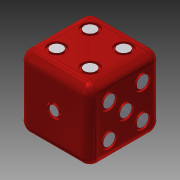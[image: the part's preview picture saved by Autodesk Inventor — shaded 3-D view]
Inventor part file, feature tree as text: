
AUTODESK INVENTOR PART (.ipt)
format: ipt  version: 2013 (Build 170138000, 138)  size: 348,160 bytes
history: native  units: mm
features: extrude x14, sketch x14, fillet x1, plane x1, mirror x1
ambient origin geometry x8: Origin, YZ Plane, XZ Plane, XY Plane, X Axis, Y Axis, Z Axis, Center Point
bodies: Solid1 (feature_tree)
feature tree (31):
  extrude  "Extrusion1"  Depth=30.0mm
  fillet  "Fillet1"  Radius=30.0mm
  extrude  "Extrusion2"  Depth=6.0mm
  extrude  "Extrusion3"  Depth=6.0mm
  plane  "Work Plane1"
  mirror  "Mirror1"
  extrude  "Extrusion4"  Depth=6.0mm
  extrude  "Extrusion5"  Depth=7.0mm
  extrude  "Extrusion6"  Depth=7.0mm
  extrude  "Extrusion7"  Depth=1.0mm TaperAngle=0.0deg
  sketch  "Sketch8"  dims[d22=7.0mm d23=7.0mm]
  sketch  "Sketch9"  dims[d24=7.0mm d25=7.0mm]
  sketch  "Sketch10"  dims[d26=1.0mm d27=0.0mm d28=14.0mm]
  sketch  "Sketch11"  dims[d29=14.0mm d30=14.0mm]
  sketch  "Sketch12"  dims[d32=14.0mm d33=4.0mm]
  sketch  "Sketch13"  dims[d34=4.0mm d35=7.0mm]
  extrude  "Extrusion8"  Depth=7.0mm
  extrude  "Extrusion9"  Depth=7.0mm
  extrude  "Extrusion10"  Depth=14.0mm
  extrude  "Extrusion11"  Depth=14.0mm
  extrude  "Extrusion12"  Depth=4.0mm
  extrude  "Extrusion13"  Depth=7.0mm
  extrude  "Extrusion14"  Depth=1.0mm TaperAngle=0.0deg
  sketch  "Sketch1"  dims[d0=30.0mm d2=30.0mm d3=30.0mm d4=0.0mm]
  sketch  "Sketch2"  dims[d5=4.0mm d6=6.0mm]
  sketch  "Sketch3"  dims[d9=1.0mm d10=0.0mm d11=6.0mm]
  sketch  "Sketch4"  dims[d13=6.0mm d14=6.0mm]
  sketch  "Sketch5"  dims[d15=7.0mm d16=7.0mm]
  sketch  "Sketch6"  dims[d17=0.0mm d18=7.0mm]
  sketch  "Sketch7"  dims[d19=0.0mm d20=1.0mm d21=0.0mm]
  sketch  "Sketch15"  dims[d36=7.0mm d37=1.0mm d38=0.0mm d39=7.0mm d40=14.0mm d42=14.0mm d43=4.0mm d44=4.0mm d45=7.0mm d46=7.0mm d47=1.0mm d48=0.0mm d49=14.0mm d51=14.0mm d52=4.0mm d53=4.0mm d54=7.0mm d55=7.0mm d56=7.0mm d57=7.0mm d58=7.0mm d59=1.0mm d60=0.0mm d61=0.0mm d62=0.0mm d63=1.0mm d64=1.0mm d65=1.0mm d66=1.0mm d67=1.0mm d68=1.0mm d69=1.0mm d70=1.0mm d71=1.0mm d72=1.0mm d73=1.0mm d74=1.0mm d75=1.0mm d76=5.0mm d77=1.0mm d78=1.0mm d79=1.0mm d80=1.0mm d81=1.0mm d82=1.0mm d85=1.0mm d86=1.0mm d87=0.0mm d88=1.0mm d89=0.0mm d90=1.0mm d91=0.0mm d92=1.0mm d93=0.0mm d94=1.0mm d95=0.0mm d96=1.0mm d97=0.0mm]
